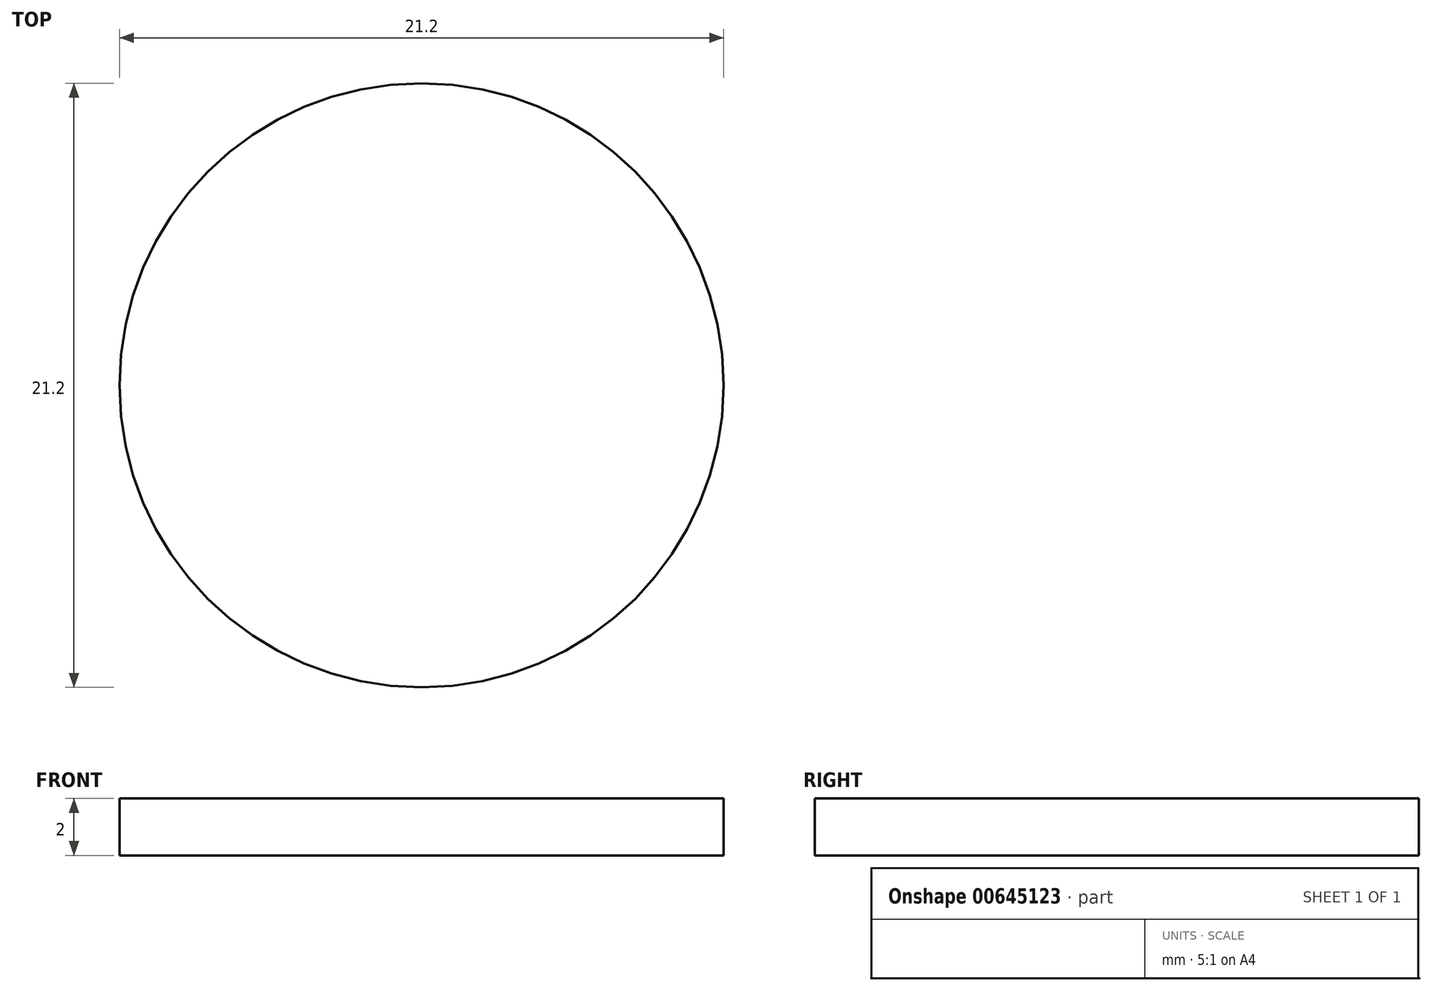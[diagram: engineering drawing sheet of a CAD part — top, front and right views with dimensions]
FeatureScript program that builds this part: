
annotation { "Feature Type Name" : "Feature", "Feature Type Description" : "" }
export const myFeature = defineFeature(function(context is Context, id is Id, definition is map)
    precondition{}
    {
        {
            var Q0;
            Q0=qCreatedBy(makeId("Top.planeOp"),FACE);
            var sketch = newSketch(context, id + "F0", { "sketchPlane" : qUnion([Q0])});
            skCircle(sketch, "E0", {"center": v(0, 0) * mm, "radius": 10.6 * mm});
            skSolve(sketch);
        }
        {
            var Q0;
            Q0=makeQuery(id+"F0.imprint","IMPRINT",FACE,{"disambiguationData":[TD([[makeQuery(id+"F0.imprint","IMPRINT",EDGE,{"derivedFrom":sQuery(id+"F0.wireOp",EDGE,"E0")}),1.0]])]});
            extrude(context, id + "F1", {"entities" : qUnion([Q0]), "depth" : 2 * mm, "offsetDistance" : 25 * mm});
        }
    });
